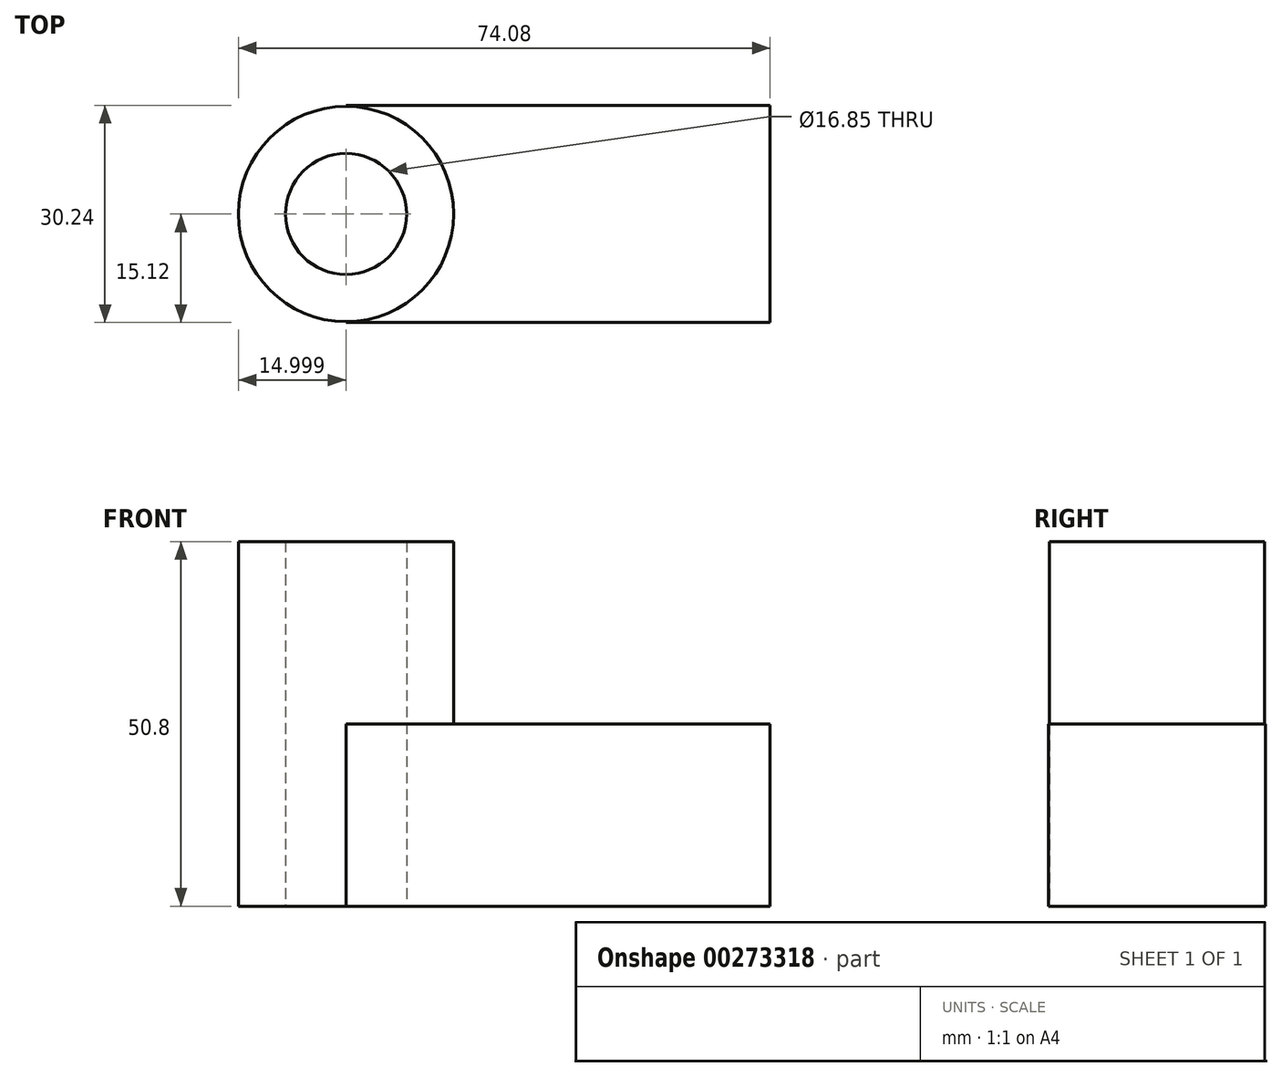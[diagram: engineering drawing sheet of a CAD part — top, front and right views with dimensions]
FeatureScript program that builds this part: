
annotation { "Feature Type Name" : "Feature", "Feature Type Description" : "" }
export const myFeature = defineFeature(function(context is Context, id is Id, definition is map)
    precondition{}
    {
        {
            var Q0;
            Q0=qCreatedBy(makeId("Top.planeOp"),FACE);
            var sketch = newSketch(context, id + "F0", { "sketchPlane" : qUnion([Q0])});
            skLineSegment(sketch, "E0.bottom", {"start": v(-29.54, 15.12) * mm, "end": v(29.54, 15.12) * mm});
            skLineSegment(sketch, "E0.top", {"start": v(-29.54, -15.12) * mm, "end": v(29.54, -15.12) * mm});
            skLineSegment(sketch, "E0.left", {"start": v(-29.54, 15.12) * mm, "end": v(-29.54, -15.12) * mm});
            skLineSegment(sketch, "E0.right", {"start": v(29.54, 15.12) * mm, "end": v(29.54, -15.12) * mm});
            skPoint(sketch, "E0.middle", {"position": v(0, 0) * mm});
            skCircle(sketch, "E1", {"center": v(-29.54, 0) * mm, "radius": 15 * mm});
            skCircle(sketch, "E2", {"center": v(-29.54, 0) * mm, "radius": 8.43 * mm});
            skSolve(sketch);
        }
        {
            var Q0;
            {var subQ0=sQuery(id+"F0.wireOp",EDGE,"E1");var subQ1=sQuery(id+"F0.wireOp",EDGE,"E0.left");var subQ2=makeQuery(id+"F0.imprint","INTERSECT",VERTEX,{"disambiguationData":[OD(0.0)],"derivedFrom":[subQ1,subQ0]});Q0=makeQuery(id+"F0.imprint","IMPRINT",FACE,{"disambiguationData":[TD([[makeQuery(id+"F0.imprint","IMPRINT",EDGE,{"disambiguationData":[TD([[subQ2,-1.0]])],"derivedFrom":subQ1}),-1.0]])]});}
            var Q1;
            {var subQ0=sQuery(id+"F0.wireOp",EDGE,"E1");var subQ1=sQuery(id+"F0.wireOp",EDGE,"E0.left");var subQ2=makeQuery(id+"F0.imprint","INTERSECT",VERTEX,{"disambiguationData":[OD(0.0)],"derivedFrom":[subQ1,subQ0]});Q1=makeQuery(id+"F0.imprint","IMPRINT",FACE,{"disambiguationData":[TD([[makeQuery(id+"F0.imprint","IMPRINT",EDGE,{"disambiguationData":[TD([[subQ2,-1.0]])],"derivedFrom":subQ1}),1.0]])]});}
            var Q2;
            {var subQ4=sQuery(id+"F0.wireOp",EDGE,"E0.bottom");Q2=makeQuery(id+"F0.imprint","IMPRINT",FACE,{"disambiguationData":[TD([[makeQuery(id+"F0.imprint","IMPRINT",EDGE,{"derivedFrom":subQ4}),-1.0]])]});}
            extrude(context, id + "F1", {"entities" : qUnion([Q0, Q1, Q2]), "depth" : 25.4 * mm});
        }
        {
            var Q0;
            {var subQ0=sQuery(id+"F0.wireOp",EDGE,"E1");var subQ1=sQuery(id+"F0.wireOp",EDGE,"E0.left");var subQ2=makeQuery(id+"F0.imprint","INTERSECT",VERTEX,{"disambiguationData":[OD(0.0)],"derivedFrom":[subQ1,subQ0]});Q0=makeQuery(id+"F0.imprint","IMPRINT",FACE,{"disambiguationData":[TD([[makeQuery(id+"F0.imprint","IMPRINT",EDGE,{"disambiguationData":[TD([[subQ2,-1.0]])],"derivedFrom":subQ1}),1.0]])]});}
            var Q1;
            {var subQ0=sQuery(id+"F0.wireOp",EDGE,"E1");var subQ1=sQuery(id+"F0.wireOp",EDGE,"E0.left");var subQ2=makeQuery(id+"F0.imprint","INTERSECT",VERTEX,{"disambiguationData":[OD(0.0)],"derivedFrom":[subQ1,subQ0]});Q1=makeQuery(id+"F0.imprint","IMPRINT",FACE,{"disambiguationData":[TD([[makeQuery(id+"F0.imprint","IMPRINT",EDGE,{"disambiguationData":[TD([[subQ2,-1.0]])],"derivedFrom":subQ1}),-1.0]])]});}
            extrude(context, id + "F2", {"entities" : qUnion([Q0, Q1]), "operationType" : NewBodyOperationType.ADD, "depth" : 50.8 * mm});
        }
    });
